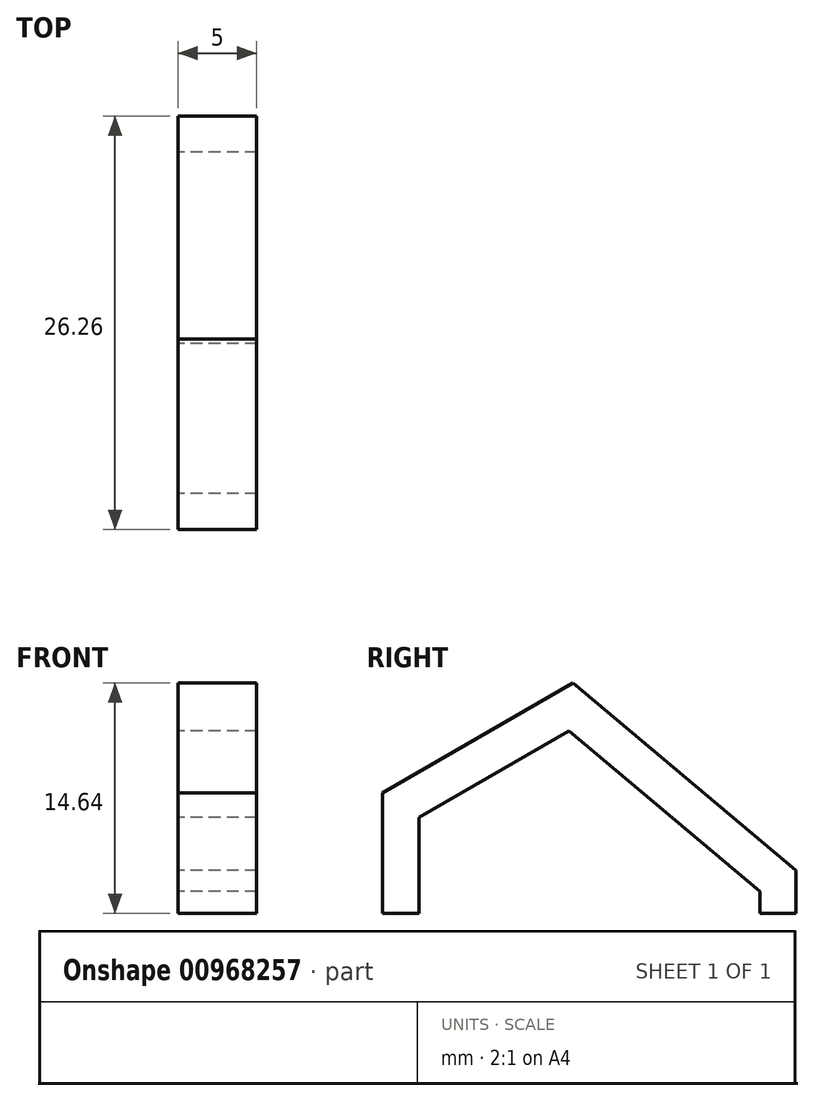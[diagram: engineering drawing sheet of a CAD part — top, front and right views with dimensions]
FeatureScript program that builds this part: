
annotation { "Feature Type Name" : "Feature", "Feature Type Description" : "" }
export const myFeature = defineFeature(function(context is Context, id is Id, definition is map)
    precondition{}
    {
        {
            var Q0;
            Q0=qCreatedBy(makeId("Right.planeOp"),FACE);
            var sketch = newSketch(context, id + "F0", { "sketchPlane" : qUnion([Q0])});
            skLineSegment(sketch, "E0", {"start": v(-11.2, 0) * mm, "end": v(-8.9, 0) * mm});
            skLineSegment(sketch, "E1", {"start": v(-11.2, 0) * mm, "end": v(-11.2, 7.66) * mm});
            skLineSegment(sketch, "E2", {"start": v(15.06, 2.75) * mm, "end": v(15.06, 0) * mm});
            skLineSegment(sketch, "E3.1", {"start": v(12.76, 1.41) * mm, "end": v(12.76, 0) * mm});
            skLineSegment(sketch, "E3.4", {"start": v(-8.9, 0) * mm, "end": v(-8.9, 6.1) * mm});
            skPoint(sketch, "E3.0.midPoint", {"position": v(7.35, 3.77) * mm});
            skLineSegment(sketch, "E4.trimOffspring", {"start": v(12.76, 0) * mm, "end": v(15.06, 0) * mm});
            skLineSegment(sketch, "E5", {"start": v(-8.9, 6.1) * mm, "end": v(0.62, 11.6) * mm});
            skLineSegment(sketch, "E6", {"start": v(0.62, 11.6) * mm, "end": v(12.76, 1.41) * mm});
            skLineSegment(sketch, "E7", {"start": v(0.62, 11.6) * mm, "end": v(0.62, 6.7) * mm, "construction": true});
            skLineSegment(sketch, "E8.0", {"start": v(0.89, 14.64) * mm, "end": v(15.06, 2.75) * mm});
            skLineSegment(sketch, "E8.1", {"start": v(-11.2, 7.66) * mm, "end": v(0.89, 14.64) * mm});
            skSolve(sketch);
        }
        {
            var Q0;
            Q0=makeQuery(id+"F0.imprint","IMPRINT",FACE,{"disambiguationData":[TD([[makeQuery(id+"F0.imprint","IMPRINT",EDGE,{"derivedFrom":sQuery(id+"F0.wireOp",EDGE,"E0")}),1.0]])]});
            extrude(context, id + "F1", {"entities" : qUnion([Q0]), "depth" : 5 * mm, "offsetDistance" : 25 * mm});
        }
    });
